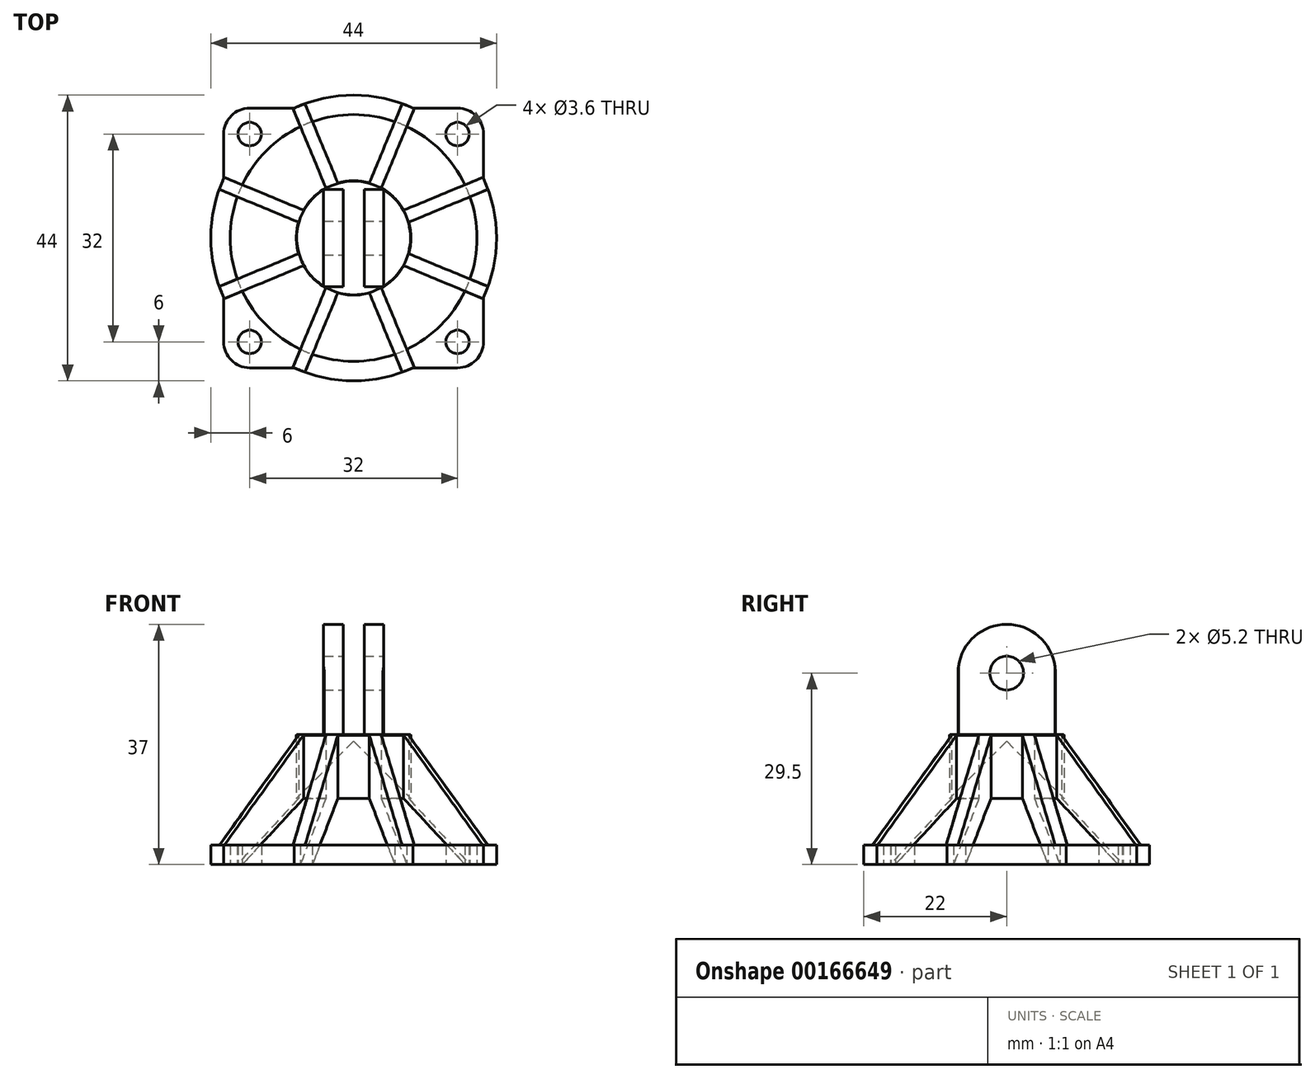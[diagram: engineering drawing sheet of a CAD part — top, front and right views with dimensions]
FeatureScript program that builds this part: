
annotation { "Feature Type Name" : "Feature", "Feature Type Description" : "" }
export const myFeature = defineFeature(function(context is Context, id is Id, definition is map)
    precondition{}
    {
        {
            var Q0;
            Q0=qCreatedBy(makeId("Top.planeOp"),FACE);
            var sketch = newSketch(context, id + "F0", { "sketchPlane" : qUnion([Q0])});
            skLineSegment(sketch, "E0.bottom", {"start": v(16, -16) * mm, "end": v(-16, -16) * mm, "construction": true});
            skLineSegment(sketch, "E0.top", {"start": v(16, 16) * mm, "end": v(-16, 16) * mm, "construction": true});
            skLineSegment(sketch, "E0.left", {"start": v(16, -16) * mm, "end": v(16, 16) * mm, "construction": true});
            skLineSegment(sketch, "E0.right", {"start": v(-16, -16) * mm, "end": v(-16, 16) * mm, "construction": true});
            skPoint(sketch, "E0.middle", {"position": v(0, 0) * mm});
            skLineSegment(sketch, "E1.bottom", {"start": v(16, -20) * mm, "end": v(9.17, -20) * mm});
            skLineSegment(sketch, "E1.top", {"start": v(16, 20) * mm, "end": v(9.17, 20) * mm});
            skLineSegment(sketch, "E1.left", {"start": v(20, -16) * mm, "end": v(20, -9.17) * mm});
            skLineSegment(sketch, "E1.right", {"start": v(-20, -16) * mm, "end": v(-20, -9.17) * mm});
            skCircle(sketch, "E2", {"center": v(0, 0) * mm, "radius": 19 * mm});
            skArc(sketch, "E3", {"start": v(-20, 9.17) * mm, "mid": v(-22, 0) * mm, "end": v(-20, -9.17) * mm});
            skLineSegment(sketch, "E4.trimOffspring", {"start": v(-9.17, 20) * mm, "end": v(-16, 20) * mm});
            skLineSegment(sketch, "E5.trimOffspring", {"start": v(20, 9.17) * mm, "end": v(20, 16) * mm});
            skLineSegment(sketch, "E6.trimOffspring", {"start": v(-9.17, -20) * mm, "end": v(-16, -20) * mm});
            skLineSegment(sketch, "E7.trimOffspring", {"start": v(-20, 9.17) * mm, "end": v(-20, 16) * mm});
            skArc(sketch, "E8.trimOffspring", {"start": v(9.17, 20) * mm, "mid": v(0, 22) * mm, "end": v(-9.17, 20) * mm});
            skArc(sketch, "E9.trimOffspring", {"start": v(20, -9.17) * mm, "mid": v(22, 0) * mm, "end": v(20, 9.17) * mm});
            skArc(sketch, "E10.trimOffspring", {"start": v(-9.17, -20) * mm, "mid": v(0, -22) * mm, "end": v(9.17, -20) * mm});
            skCircle(sketch, "E11", {"center": v(-16, 16) * mm, "radius": 1.8 * mm});
            skCircle(sketch, "E12", {"center": v(16, 16) * mm, "radius": 1.8 * mm});
            skCircle(sketch, "E13", {"center": v(16, -16) * mm, "radius": 1.8 * mm});
            skCircle(sketch, "E14", {"center": v(-16, -16) * mm, "radius": 1.8 * mm});
            skArc(sketch, "E15", {"start": v(20, 16) * mm, "mid": v(18.83, 18.83) * mm, "end": v(16, 20) * mm});
            skArc(sketch, "E16", {"start": v(-16, 20) * mm, "mid": v(-18.83, 18.83) * mm, "end": v(-20, 16) * mm});
            skArc(sketch, "E17", {"start": v(-20, -16) * mm, "mid": v(-18.83, -18.83) * mm, "end": v(-16, -20) * mm});
            skArc(sketch, "E18", {"start": v(16, -20) * mm, "mid": v(18.83, -18.83) * mm, "end": v(20, -16) * mm});
            skPoint(sketch, "E19.orphan", {"position": v(20, 20) * mm});
            skPoint(sketch, "E20.orphan", {"position": v(-20, 20) * mm});
            skPoint(sketch, "E21.orphan", {"position": v(-20, -20) * mm});
            skPoint(sketch, "E22.orphan", {"position": v(20, -20) * mm});
            skSolve(sketch);
        }
        {
            var Q0;
            Q0 = qSketchRegion(id + "F0", true);
            extrude(context, id + "F1", {"entities" : qUnion([Q0]), "depth" : 3 * mm});
        }
        {
            var Q0;
            Q0=qCreatedBy(makeId("Top.planeOp"),FACE);
            var sketch = newSketch(context, id + "F2", { "sketchPlane" : qUnion([Q0])});
            skLineSegment(sketch, "E23.bottom", {"start": v(7.5, -7.5) * mm, "end": v(-7.5, -7.5) * mm});
            skLineSegment(sketch, "E23.top", {"start": v(7.5, 7.5) * mm, "end": v(-7.5, 7.5) * mm});
            skLineSegment(sketch, "E23.left", {"start": v(7.5, -7.5) * mm, "end": v(7.5, 7.5) * mm});
            skLineSegment(sketch, "E23.right", {"start": v(-7.5, -7.5) * mm, "end": v(-7.5, 7.5) * mm});
            skPoint(sketch, "E23.middle", {"position": v(0, 0) * mm});
            skLineSegment(sketch, "E24", {"start": v(0, 0) * mm, "end": v(-20.33, 8.42) * mm, "construction": true});
            skCircle(sketch, "E25", {"center": v(0, 0) * mm, "radius": 22 * mm});
            skCircle(sketch, "E26", {"center": v(0, 0) * mm, "radius": 8.81 * mm});
            skLineSegment(sketch, "E27", {"start": v(-8.47, 2.43) * mm, "end": v(-20.69, 7.49) * mm});
            skLineSegment(sketch, "E28", {"start": v(-7.7, 4.27) * mm, "end": v(-19.92, 9.33) * mm});
            skLineSegment(sketch, "E29.1.1", {"start": v(-7.7, -4.27) * mm, "end": v(-19.92, -9.33) * mm});
            skLineSegment(sketch, "E29.1.2", {"start": v(-8.47, -2.43) * mm, "end": v(-20.69, -7.49) * mm});
            skLineSegment(sketch, "E29.2.1", {"start": v(-2.43, -8.47) * mm, "end": v(-7.49, -20.69) * mm});
            skLineSegment(sketch, "E29.2.2", {"start": v(-4.27, -7.7) * mm, "end": v(-9.33, -19.92) * mm});
            skLineSegment(sketch, "E29.3.1", {"start": v(4.27, -7.7) * mm, "end": v(9.33, -19.92) * mm});
            skLineSegment(sketch, "E29.3.2", {"start": v(2.43, -8.47) * mm, "end": v(7.49, -20.69) * mm});
            skLineSegment(sketch, "E29.4.1", {"start": v(8.47, -2.43) * mm, "end": v(20.69, -7.49) * mm});
            skLineSegment(sketch, "E29.4.2", {"start": v(7.7, -4.27) * mm, "end": v(19.92, -9.33) * mm});
            skLineSegment(sketch, "E29.5.1", {"start": v(7.7, 4.27) * mm, "end": v(19.92, 9.33) * mm});
            skLineSegment(sketch, "E29.5.2", {"start": v(8.47, 2.43) * mm, "end": v(20.69, 7.49) * mm});
            skLineSegment(sketch, "E29.6.1", {"start": v(2.43, 8.47) * mm, "end": v(7.49, 20.69) * mm});
            skLineSegment(sketch, "E29.6.2", {"start": v(4.27, 7.7) * mm, "end": v(9.33, 19.92) * mm});
            skLineSegment(sketch, "E29.7.1", {"start": v(-4.27, 7.7) * mm, "end": v(-9.33, 19.92) * mm});
            skLineSegment(sketch, "E29.7.2", {"start": v(-2.43, 8.47) * mm, "end": v(-7.49, 20.69) * mm});
            skArc(sketch, "E30.0", {"start": v(-20, 9.17) * mm, "mid": v(-22, 0) * mm, "end": v(-20, -9.17) * mm, "construction": true});
            skLineSegment(sketch, "E31", {"start": v(-1.63, 7.5) * mm, "end": v(-1.62, -7.5) * mm, "construction": true});
            skLineSegment(sketch, "E32", {"start": v(-4.62, 7.5) * mm, "end": v(-4.62, -7.5) * mm, "construction": true});
            skPoint(sketch, "E33", {"position": v(0, 7.5) * mm});
            skSolve(sketch);
        }
        {
            var Q0;
            {var subQ0=sQuery(id+"F2.wireOp",EDGE,"E29.7.1");Q0=makeQuery(id+"F2.imprint","IMPRINT",FACE,{"disambiguationData":[TD([[makeQuery(id+"F2.imprint","IMPRINT",EDGE,{"derivedFrom":subQ0}),-1.0]])]});}
            var Q1;
            {var subQ0=sQuery(id+"F2.wireOp",EDGE,"E27");Q1=makeQuery(id+"F2.imprint","IMPRINT",FACE,{"disambiguationData":[TD([[makeQuery(id+"F2.imprint","IMPRINT",EDGE,{"derivedFrom":subQ0}),-1.0]])]});}
            var Q2;
            {var subQ0=sQuery(id+"F2.wireOp",EDGE,"E29.1.1");Q2=makeQuery(id+"F2.imprint","IMPRINT",FACE,{"disambiguationData":[TD([[makeQuery(id+"F2.imprint","IMPRINT",EDGE,{"derivedFrom":subQ0}),-1.0]])]});}
            var Q3;
            {var subQ0=sQuery(id+"F2.wireOp",EDGE,"E29.2.1");Q3=makeQuery(id+"F2.imprint","IMPRINT",FACE,{"disambiguationData":[TD([[makeQuery(id+"F2.imprint","IMPRINT",EDGE,{"derivedFrom":subQ0}),-1.0]])]});}
            var Q4;
            {var subQ0=sQuery(id+"F2.wireOp",EDGE,"E29.3.1");Q4=makeQuery(id+"F2.imprint","IMPRINT",FACE,{"disambiguationData":[TD([[makeQuery(id+"F2.imprint","IMPRINT",EDGE,{"derivedFrom":subQ0}),-1.0]])]});}
            var Q5;
            {var subQ0=sQuery(id+"F2.wireOp",EDGE,"E29.4.1");Q5=makeQuery(id+"F2.imprint","IMPRINT",FACE,{"disambiguationData":[TD([[makeQuery(id+"F2.imprint","IMPRINT",EDGE,{"derivedFrom":subQ0}),-1.0]])]});}
            var Q6;
            {var subQ0=sQuery(id+"F2.wireOp",EDGE,"E29.5.1");Q6=makeQuery(id+"F2.imprint","IMPRINT",FACE,{"disambiguationData":[TD([[makeQuery(id+"F2.imprint","IMPRINT",EDGE,{"derivedFrom":subQ0}),-1.0]])]});}
            var Q7;
            {var subQ0=sQuery(id+"F2.wireOp",EDGE,"E29.6.1");Q7=makeQuery(id+"F2.imprint","IMPRINT",FACE,{"disambiguationData":[TD([[makeQuery(id+"F2.imprint","IMPRINT",EDGE,{"derivedFrom":subQ0}),-1.0]])]});}
            var Q8;
            {var subQ0=sQuery(id+"F2.wireOp",EDGE,"E26");var subQ8=sQuery(id+"F2.wireOp",EDGE,"E23.bottom");var subQ9=makeQuery(id+"F2.imprint","INTERSECT",VERTEX,{"disambiguationData":[OD(0.0)],"derivedFrom":[subQ8,subQ0]});Q8=makeQuery(id+"F2.imprint","IMPRINT",FACE,{"disambiguationData":[TD([[makeQuery(id+"F2.imprint","IMPRINT",EDGE,{"disambiguationData":[TD([[subQ9,-1.0]])],"derivedFrom":subQ8}),-1.0]])]});}
            var Q9;
            {var subQ0=sQuery(id+"F2.wireOp",EDGE,"E26");var subQ4=sQuery(id+"F2.wireOp",EDGE,"E23.top");var subQ5=makeQuery(id+"F2.imprint","INTERSECT",VERTEX,{"disambiguationData":[OD(0.0)],"derivedFrom":[subQ4,subQ0]});Q9=makeQuery(id+"F2.imprint","IMPRINT",FACE,{"disambiguationData":[TD([[makeQuery(id+"F2.imprint","IMPRINT",EDGE,{"disambiguationData":[TD([[subQ5,-1.0]])],"derivedFrom":subQ4}),-1.0]])]});}
            var Q10;
            {var subQ0=sQuery(id+"F2.wireOp",EDGE,"E26");var subQ2=sQuery(id+"F2.wireOp",EDGE,"E23.left");var subQ3=makeQuery(id+"F2.imprint","INTERSECT",VERTEX,{"disambiguationData":[OD(0.0)],"derivedFrom":[subQ2,subQ0]});Q10=makeQuery(id+"F2.imprint","IMPRINT",FACE,{"disambiguationData":[TD([[makeQuery(id+"F2.imprint","IMPRINT",EDGE,{"disambiguationData":[TD([[subQ3,-1.0]])],"derivedFrom":subQ2}),-1.0]])]});}
            var Q11;
            {var subQ0=sQuery(id+"F2.wireOp",EDGE,"E26");var subQ5=sQuery(id+"F2.wireOp",EDGE,"E23.bottom");var subQ7=makeQuery(id+"F2.imprint","INTERSECT",VERTEX,{"disambiguationData":[OD(0.0)],"derivedFrom":[subQ5,subQ0]});Q11=makeQuery(id+"F2.imprint","IMPRINT",FACE,{"disambiguationData":[TD([[makeQuery(id+"F2.imprint","IMPRINT",EDGE,{"disambiguationData":[TD([[subQ7,-1.0]])],"derivedFrom":subQ5}),1.0]])]});}
            var Q12;
            {var subQ0=sQuery(id+"F2.wireOp",EDGE,"E26");var subQ4=sQuery(id+"F2.wireOp",EDGE,"E23.right");var subQ6=makeQuery(id+"F2.imprint","INTERSECT",VERTEX,{"disambiguationData":[OD(0.0)],"derivedFrom":[subQ4,subQ0]});Q12=makeQuery(id+"F2.imprint","IMPRINT",FACE,{"disambiguationData":[TD([[makeQuery(id+"F2.imprint","IMPRINT",EDGE,{"disambiguationData":[TD([[subQ6,-1.0]])],"derivedFrom":subQ4}),1.0]])]});}
            extrude(context, id + "F3", {"entities" : qUnion([Q0, Q1, Q2, Q3, Q4, Q5, Q6, Q7, Q8, Q9, Q10, Q11, Q12]), "operationType" : NewBodyOperationType.ADD, "depth" : 20 * mm});
        }
        {
            var Q0;
            Q0=qCreatedBy(makeId("Front.planeOp"),FACE);
            var sketch = newSketch(context, id + "F4", { "sketchPlane" : qUnion([Q0])});
            skPoint(sketch, "E34.0", {"position": v(0, 0) * mm});
            skPoint(sketch, "E34.1", {"position": v(-19, 0) * mm});
            skLineSegment(sketch, "E35", {"start": v(-19, 0) * mm, "end": v(0, 0) * mm});
            skLineSegment(sketch, "E36", {"start": v(0, 0) * mm, "end": v(0, 19) * mm});
            skLineSegment(sketch, "E37", {"start": v(0, 19) * mm, "end": v(-19, 0) * mm});
            skSolve(sketch);
        }
        {
            var Q0;
            Q0=makeQuery(id+"F4.imprint","IMPRINT",FACE,{"disambiguationData":[TD([[makeQuery(id+"F4.imprint","IMPRINT",EDGE,{"derivedFrom":sQuery(id+"F4.wireOp",EDGE,"E35")}),1.0]])]});
            var Q1;
            Q1=sQuery(id+"F4.wireOp",EDGE,"E36");
            revolve(context, id + "F5", {"operationType" : NewBodyOperationType.REMOVE, "entities" : qUnion([Q0]), "axis" : qUnion([Q1]), "revolveType" : RevolveType.FULL, "oppositeDirection" : true});
        }
        {
            var Q0;
            Q0=makeQuery(id+"F3.opExtrude","SWEPT_FACE",FACE,{"disambiguationData":[OSD([sQuery(id+"F2.wireOp",EDGE,"E29.2.1")])]});
            var Q1;
            Q1=makeQuery(id+"F3.opExtrude","SWEPT_FACE",FACE,{"disambiguationData":[OSD([sQuery(id+"F2.wireOp",EDGE,"E29.2.2")])]});
            cPlane(context, id + "F6", {"entities" : qUnion([Q0, Q1]), "cplaneType" : CPlaneType.MID_PLANE, "offset" : 25 * mm, "width" : 150 * mm, "height" : 150 * mm});
        }
        {
            var Q0;
            Q0=qCreatedBy(id+"F6.planeOp",FACE);
            var sketch = newSketch(context, id + "F7", { "sketchPlane" : qUnion([Q0])});
            skPoint(sketch, "E38.0", {"position": v(-21.98, 3) * mm});
            skPoint(sketch, "E38.1", {"position": v(-8.75, 20) * mm});
            skPoint(sketch, "E39.0", {"position": v(-21.98, 20) * mm});
            skLineSegment(sketch, "E40", {"start": v(0, 0) * mm, "end": v(0, 20.24) * mm, "construction": true});
            skLineSegment(sketch, "E41", {"start": v(-21.98, 3) * mm, "end": v(-8.75, 20) * mm});
            skLineSegment(sketch, "E42", {"start": v(-21.98, 20) * mm, "end": v(-8.75, 20) * mm});
            skLineSegment(sketch, "E43", {"start": v(-21.98, 3) * mm, "end": v(-22.48, 3) * mm});
            skLineSegment(sketch, "E44", {"start": v(-22.48, 3) * mm, "end": v(-22.48, 20) * mm});
            skLineSegment(sketch, "E45", {"start": v(-22.48, 20) * mm, "end": v(-21.98, 20) * mm});
            skSolve(sketch);
        }
        {
            var Q0;
            Q0=makeQuery(id+"F7.imprint","IMPRINT",FACE,{"disambiguationData":[TD([[makeQuery(id+"F7.imprint","IMPRINT",EDGE,{"derivedFrom":sQuery(id+"F7.wireOp",EDGE,"E41")}),1.0]])]});
            var Q1;
            Q1=sQuery(id+"F7.wireOp",EDGE,"E40");
            revolve(context, id + "F8", {"operationType" : NewBodyOperationType.REMOVE, "entities" : qUnion([Q0]), "axis" : qUnion([Q1]), "revolveType" : RevolveType.FULL, "oppositeDirection" : true});
        }
        {
            var Q0;
            {var subQ0=sQuery(id+"F2.wireOp",EDGE,"E26");var subQ1=sQuery(id+"F2.wireOp",EDGE,"E25");Q0=makeQuery(id+"FryXNGp9iaOWU7Y_1.boolean.opBoolean","MERGE",FACE,{"derivedFrom":[makeQuery(id+"F3.opExtrude","CAP_FACE",FACE,{"disambiguationData":[OSD([subQ1,subQ0,sQuery(id+"F2.wireOp",EDGE,"E29.5.1"),sQuery(id+"F2.wireOp",EDGE,"E29.5.2")])],"isStart":false}),makeQuery(id+"F3.opExtrude","CAP_FACE",FACE,{"disambiguationData":[OSD([subQ1,subQ0,sQuery(id+"F2.wireOp",EDGE,"E29.6.1"),sQuery(id+"F2.wireOp",EDGE,"E29.6.2")])],"isStart":false}),makeQuery(id+"F3.opExtrude","CAP_FACE",FACE,{"disambiguationData":[OSD([subQ1,subQ0,sQuery(id+"F2.wireOp",EDGE,"E29.7.1"),sQuery(id+"F2.wireOp",EDGE,"E29.7.2")])],"isStart":false}),makeQuery(id+"F3.opExtrude","CAP_FACE",FACE,{"disambiguationData":[OSD([subQ1,subQ0,sQuery(id+"F2.wireOp",EDGE,"E27"),sQuery(id+"F2.wireOp",EDGE,"E28")])],"isStart":false}),makeQuery(id+"F3.opExtrude","CAP_FACE",FACE,{"disambiguationData":[OSD([subQ1,subQ0,sQuery(id+"F2.wireOp",EDGE,"E29.1.1"),sQuery(id+"F2.wireOp",EDGE,"E29.1.2")])],"isStart":false}),makeQuery(id+"F3.opExtrude","CAP_FACE",FACE,{"disambiguationData":[OSD([subQ1,subQ0,sQuery(id+"F2.wireOp",EDGE,"E29.2.1"),sQuery(id+"F2.wireOp",EDGE,"E29.2.2")])],"isStart":false}),makeQuery(id+"F3.opExtrude","CAP_FACE",FACE,{"disambiguationData":[OSD([subQ1,subQ0,sQuery(id+"F2.wireOp",EDGE,"E29.3.1"),sQuery(id+"F2.wireOp",EDGE,"E29.3.2")])],"isStart":false}),makeQuery(id+"F3.opExtrude","CAP_FACE",FACE,{"disambiguationData":[OSD([subQ1,subQ0,sQuery(id+"F2.wireOp",EDGE,"E29.4.1"),sQuery(id+"F2.wireOp",EDGE,"E29.4.2")])],"isStart":false}),makeQuery(id+"FryXNGp9iaOWU7Y_1.opExtrude","CAP_FACE",FACE,{"disambiguationData":[OSD([subQ0])],"isStart":false})]});}
            var sketch = newSketch(context, id + "F9", { "sketchPlane" : qUnion([Q0])});
            skLineSegment(sketch, "E46.0", {"start": v(-7.5, -7.5) * mm, "end": v(-7.5, 7.5) * mm});
            skLineSegment(sketch, "E46.1", {"start": v(7.5, -7.5) * mm, "end": v(-7.5, -7.5) * mm});
            skLineSegment(sketch, "E46.2", {"start": v(7.5, -7.5) * mm, "end": v(7.5, 7.5) * mm});
            skLineSegment(sketch, "E46.3", {"start": v(7.5, 7.5) * mm, "end": v(-7.5, 7.5) * mm});
            skPoint(sketch, "E46.4", {"position": v(0, 0) * mm});
            skLineSegment(sketch, "E47", {"start": v(-1.62, 7.5) * mm, "end": v(-1.63, -7.5) * mm});
            skLineSegment(sketch, "E48", {"start": v(-4.62, 7.5) * mm, "end": v(-4.63, -7.5) * mm});
            skLineSegment(sketch, "E49", {"start": v(1.62, 7.5) * mm, "end": v(1.63, -7.5) * mm});
            skLineSegment(sketch, "E50", {"start": v(4.62, 7.5) * mm, "end": v(4.63, -7.5) * mm});
            skSolve(sketch);
        }
        {
            var Q0;
            {var subQ0=sQuery(id+"F9.wireOp",EDGE,"E47");var subQ1=sQuery(id+"F9.wireOp",EDGE,"E46.3");var subQ2=makeQuery(id+"F9.imprint","INTERSECT",VERTEX,{"derivedFrom":[subQ1,subQ0]});Q0=makeQuery(id+"F9.imprint","IMPRINT",FACE,{"disambiguationData":[TD([[makeQuery(id+"F9.imprint","IMPRINT",EDGE,{"disambiguationData":[TD([[subQ2,-1.0]])],"derivedFrom":subQ1}),1.0]])]});}
            var Q1;
            {var subQ0=sQuery(id+"F9.wireOp",EDGE,"E47");var subQ1=sQuery(id+"F2.wireOp",EDGE,"E26");var subQ2=sQuery(id+"F2.wireOp",EDGE,"E25");var subQ3=sQuery(id+"F2.wireOp",EDGE,"E29.2.2");var subQ4=sQuery(id+"F2.wireOp",EDGE,"E29.2.1");var subQ5=sQuery(id+"F2.wireOp",EDGE,"E29.7.2");var subQ6=sQuery(id+"F2.wireOp",EDGE,"E29.7.1");var subQ7=makeQuery(id+"FryXNGp9iaOWU7Y_1.boolean.opBoolean","MERGE",FACE,{"derivedFrom":[makeQuery(id+"F3.opExtrude","CAP_FACE",FACE,{"disambiguationData":[OSD([subQ2,subQ1,sQuery(id+"F2.wireOp",EDGE,"E29.5.1"),sQuery(id+"F2.wireOp",EDGE,"E29.5.2")])],"isStart":false}),makeQuery(id+"F3.opExtrude","CAP_FACE",FACE,{"disambiguationData":[OSD([subQ2,subQ1,sQuery(id+"F2.wireOp",EDGE,"E29.6.1"),sQuery(id+"F2.wireOp",EDGE,"E29.6.2")])],"isStart":false}),makeQuery(id+"F3.opExtrude","CAP_FACE",FACE,{"disambiguationData":[OSD([subQ2,subQ1,subQ6,subQ5])],"isStart":false}),makeQuery(id+"F3.opExtrude","CAP_FACE",FACE,{"disambiguationData":[OSD([subQ2,subQ1,sQuery(id+"F2.wireOp",EDGE,"E27"),sQuery(id+"F2.wireOp",EDGE,"E28")])],"isStart":false}),makeQuery(id+"F3.opExtrude","CAP_FACE",FACE,{"disambiguationData":[OSD([subQ2,subQ1,sQuery(id+"F2.wireOp",EDGE,"E29.1.1"),sQuery(id+"F2.wireOp",EDGE,"E29.1.2")])],"isStart":false}),makeQuery(id+"F3.opExtrude","CAP_FACE",FACE,{"disambiguationData":[OSD([subQ2,subQ1,subQ4,subQ3])],"isStart":false}),makeQuery(id+"F3.opExtrude","CAP_FACE",FACE,{"disambiguationData":[OSD([subQ2,subQ1,sQuery(id+"F2.wireOp",EDGE,"E29.3.1"),sQuery(id+"F2.wireOp",EDGE,"E29.3.2")])],"isStart":false}),makeQuery(id+"F3.opExtrude","CAP_FACE",FACE,{"disambiguationData":[OSD([subQ2,subQ1,sQuery(id+"F2.wireOp",EDGE,"E29.4.1"),sQuery(id+"F2.wireOp",EDGE,"E29.4.2")])],"isStart":false}),makeQuery(id+"FryXNGp9iaOWU7Y_1.opExtrude","CAP_FACE",FACE,{"disambiguationData":[OSD([subQ1])],"isStart":false})]});var subQ8=makeQuery(id+"FLweHT1gDxulgPf_1.opChamfer","BLEND_EDGE",EDGE,{"blendedFrom":[makeQuery(id+"F3.opExtrude","CAP_EDGE",EDGE,{"disambiguationData":[OSD([subQ2]),TDD([makeQuery(id+"F2.imprint","IMPRINT",EDGE,{"disambiguationData":[TD([[makeQuery(id+"F2.imprint","INTERSECT",VERTEX,{"derivedFrom":[subQ2,subQ6]}),1.0]])],"derivedFrom":subQ2})])],"isStart":false}),subQ7],"blendedInto":[subQ7]});var subQ9=makeQuery(id+"F9.imprint","INTERSECT",VERTEX,{"derivedFrom":[subQ8,subQ0]});Q1=makeQuery(id+"F9.imprint","IMPRINT",FACE,{"disambiguationData":[TD([[makeQuery(id+"F9.imprint","IMPRINT",EDGE,{"disambiguationData":[TD([[subQ9,-1.0]])],"derivedFrom":subQ0}),-1.0]])]});}
            var Q2;
            {var subQ0=sQuery(id+"F9.wireOp",EDGE,"E47");var subQ1=sQuery(id+"F9.wireOp",EDGE,"E46.1");var subQ2=makeQuery(id+"F9.imprint","INTERSECT",VERTEX,{"derivedFrom":[subQ1,subQ0]});Q2=makeQuery(id+"F9.imprint","IMPRINT",FACE,{"disambiguationData":[TD([[makeQuery(id+"F9.imprint","IMPRINT",EDGE,{"disambiguationData":[TD([[subQ2,-1.0]])],"derivedFrom":subQ1}),-1.0]])]});}
            var Q3;
            {var subQ0=sQuery(id+"F9.wireOp",EDGE,"E49");var subQ1=sQuery(id+"F2.wireOp",EDGE,"E26");var subQ2=sQuery(id+"F2.wireOp",EDGE,"E25");var subQ3=sQuery(id+"F2.wireOp",EDGE,"E29.3.2");var subQ4=sQuery(id+"F2.wireOp",EDGE,"E29.3.1");var subQ5=sQuery(id+"F2.wireOp",EDGE,"E29.6.2");var subQ6=sQuery(id+"F2.wireOp",EDGE,"E29.6.1");var subQ7=makeQuery(id+"FryXNGp9iaOWU7Y_1.boolean.opBoolean","MERGE",FACE,{"derivedFrom":[makeQuery(id+"F3.opExtrude","CAP_FACE",FACE,{"disambiguationData":[OSD([subQ2,subQ1,sQuery(id+"F2.wireOp",EDGE,"E29.5.1"),sQuery(id+"F2.wireOp",EDGE,"E29.5.2")])],"isStart":false}),makeQuery(id+"F3.opExtrude","CAP_FACE",FACE,{"disambiguationData":[OSD([subQ2,subQ1,subQ6,subQ5])],"isStart":false}),makeQuery(id+"F3.opExtrude","CAP_FACE",FACE,{"disambiguationData":[OSD([subQ2,subQ1,sQuery(id+"F2.wireOp",EDGE,"E29.7.1"),sQuery(id+"F2.wireOp",EDGE,"E29.7.2")])],"isStart":false}),makeQuery(id+"F3.opExtrude","CAP_FACE",FACE,{"disambiguationData":[OSD([subQ2,subQ1,sQuery(id+"F2.wireOp",EDGE,"E27"),sQuery(id+"F2.wireOp",EDGE,"E28")])],"isStart":false}),makeQuery(id+"F3.opExtrude","CAP_FACE",FACE,{"disambiguationData":[OSD([subQ2,subQ1,sQuery(id+"F2.wireOp",EDGE,"E29.1.1"),sQuery(id+"F2.wireOp",EDGE,"E29.1.2")])],"isStart":false}),makeQuery(id+"F3.opExtrude","CAP_FACE",FACE,{"disambiguationData":[OSD([subQ2,subQ1,sQuery(id+"F2.wireOp",EDGE,"E29.2.1"),sQuery(id+"F2.wireOp",EDGE,"E29.2.2")])],"isStart":false}),makeQuery(id+"F3.opExtrude","CAP_FACE",FACE,{"disambiguationData":[OSD([subQ2,subQ1,subQ4,subQ3])],"isStart":false}),makeQuery(id+"F3.opExtrude","CAP_FACE",FACE,{"disambiguationData":[OSD([subQ2,subQ1,sQuery(id+"F2.wireOp",EDGE,"E29.4.1"),sQuery(id+"F2.wireOp",EDGE,"E29.4.2")])],"isStart":false}),makeQuery(id+"FryXNGp9iaOWU7Y_1.opExtrude","CAP_FACE",FACE,{"disambiguationData":[OSD([subQ1])],"isStart":false})]});var subQ8=makeQuery(id+"FLweHT1gDxulgPf_1.opChamfer","BLEND_EDGE",EDGE,{"blendedFrom":[makeQuery(id+"F3.opExtrude","CAP_EDGE",EDGE,{"disambiguationData":[OSD([subQ2]),TDD([makeQuery(id+"F2.imprint","IMPRINT",EDGE,{"disambiguationData":[TD([[makeQuery(id+"F2.imprint","INTERSECT",VERTEX,{"derivedFrom":[subQ2,subQ6]}),1.0]])],"derivedFrom":subQ2})])],"isStart":false}),subQ7],"blendedInto":[subQ7]});var subQ9=makeQuery(id+"F9.imprint","INTERSECT",VERTEX,{"derivedFrom":[subQ8,subQ0]});Q3=makeQuery(id+"F9.imprint","IMPRINT",FACE,{"disambiguationData":[TD([[makeQuery(id+"F9.imprint","IMPRINT",EDGE,{"disambiguationData":[TD([[subQ9,-1.0]])],"derivedFrom":subQ0}),1.0]])]});}
            var Q4;
            {var subQ0=sQuery(id+"F9.wireOp",EDGE,"E49");var subQ1=sQuery(id+"F9.wireOp",EDGE,"E46.3");var subQ2=makeQuery(id+"F9.imprint","INTERSECT",VERTEX,{"derivedFrom":[subQ1,subQ0]});Q4=makeQuery(id+"F9.imprint","IMPRINT",FACE,{"disambiguationData":[TD([[makeQuery(id+"F9.imprint","IMPRINT",EDGE,{"disambiguationData":[TD([[subQ2,1.0]])],"derivedFrom":subQ1}),1.0]])]});}
            var Q5;
            {var subQ0=sQuery(id+"F9.wireOp",EDGE,"E49");var subQ1=sQuery(id+"F9.wireOp",EDGE,"E46.1");var subQ2=makeQuery(id+"F9.imprint","INTERSECT",VERTEX,{"derivedFrom":[subQ1,subQ0]});Q5=makeQuery(id+"F9.imprint","IMPRINT",FACE,{"disambiguationData":[TD([[makeQuery(id+"F9.imprint","IMPRINT",EDGE,{"disambiguationData":[TD([[subQ2,1.0]])],"derivedFrom":subQ1}),-1.0]])]});}
            var Q6;
            Q6=makeQuery(id+"F1.opExtrude","SWEPT_BODY",BODY,{"disambiguationData":[OSD([sQuery(id+"F0.wireOp",EDGE,"E1.bottom"),sQuery(id+"F0.wireOp",EDGE,"E1.top"),sQuery(id+"F0.wireOp",EDGE,"E1.left"),sQuery(id+"F0.wireOp",EDGE,"E1.right"),sQuery(id+"F0.wireOp",EDGE,"E2"),sQuery(id+"F0.wireOp",EDGE,"E3"),sQuery(id+"F0.wireOp",EDGE,"E4.trimOffspring"),sQuery(id+"F0.wireOp",EDGE,"E5.trimOffspring"),sQuery(id+"F0.wireOp",EDGE,"E6.trimOffspring"),sQuery(id+"F0.wireOp",EDGE,"E7.trimOffspring"),sQuery(id+"F0.wireOp",EDGE,"E8.trimOffspring"),sQuery(id+"F0.wireOp",EDGE,"E9.trimOffspring"),sQuery(id+"F0.wireOp",EDGE,"E10.trimOffspring"),sQuery(id+"F0.wireOp",EDGE,"E11"),sQuery(id+"F0.wireOp",EDGE,"E12"),sQuery(id+"F0.wireOp",EDGE,"E13"),sQuery(id+"F0.wireOp",EDGE,"E14"),sQuery(id+"F0.wireOp",EDGE,"E15"),sQuery(id+"F0.wireOp",EDGE,"E16"),sQuery(id+"F0.wireOp",EDGE,"E17"),sQuery(id+"F0.wireOp",EDGE,"E18")])]});
            extrude(context, id + "F10", {"entities" : qUnion([Q0, Q1, Q2, Q3, Q4, Q5]), "operationType" : NewBodyOperationType.ADD, "depth" : 17 * mm, "hasSecondDirection" : true, "secondDirectionOppositeDirection" : true, "secondDirectionBoundEntityBody" : qUnion([Q6]), "secondDirectionDepth" : 1 * mm});
        }
        {
            var Q0;
            Q0=makeQuery(id+"F10.opExtrude","SWEPT_FACE",FACE,{"disambiguationData":[OSD([sQuery(id+"F9.wireOp",EDGE,"E50")])]});
            var sketch = newSketch(context, id + "F11", { "sketchPlane" : qUnion([Q0])});
            skCircle(sketch, "E51", {"center": v(0, 29.5) * mm, "radius": 7.5 * mm});
            skPoint(sketch, "E51.centerSnap0", {"position": v(0, 37) * mm});
            skCircle(sketch, "E52", {"center": v(0, 29.5) * mm, "radius": 2.6 * mm});
            skLineSegment(sketch, "E53", {"start": v(-7.5, 29.5) * mm, "end": v(-7.5, 37) * mm});
            skLineSegment(sketch, "E54", {"start": v(-7.5, 37) * mm, "end": v(-7.43, 37) * mm});
            skLineSegment(sketch, "E55", {"start": v(7.5, 29.5) * mm, "end": v(7.5, 37) * mm});
            skLineSegment(sketch, "E56", {"start": v(7.5, 37) * mm, "end": v(7.43, 37) * mm});
            skSolve(sketch);
        }
        {
            var Q0;
            {var subQ0=sQuery(id+"F11.wireOp",EDGE,"E51");var subQ1=sQuery(id+"F9.wireOp",EDGE,"E50");var subQ2=makeQuery(id+"F10.opExtrude","CAP_EDGE",EDGE,{"disambiguationData":[OSD([subQ1])],"isStart":false});var subQ3=makeQuery(id+"F11.imprint","INTERSECT",VERTEX,{"derivedFrom":[subQ2,subQ0]});Q0=makeQuery(id+"F11.imprint","IMPRINT",FACE,{"disambiguationData":[TD([[makeQuery(id+"F11.imprint","IMPRINT",EDGE,{"disambiguationData":[TD([[subQ3,-1.0]])],"derivedFrom":subQ0}),-1.0]])]});}
            var Q1;
            {var subQ0=sQuery(id+"F11.wireOp",EDGE,"E51");var subQ1=sQuery(id+"F9.wireOp",EDGE,"E50");var subQ2=makeQuery(id+"F10.opExtrude","CAP_EDGE",EDGE,{"disambiguationData":[OSD([subQ1])],"isStart":false});var subQ3=makeQuery(id+"F11.imprint","INTERSECT",VERTEX,{"derivedFrom":[subQ2,subQ0]});Q1=makeQuery(id+"F11.imprint","IMPRINT",FACE,{"disambiguationData":[TD([[makeQuery(id+"F11.imprint","IMPRINT",EDGE,{"disambiguationData":[TD([[subQ3,1.0]])],"derivedFrom":subQ0}),-1.0]])]});}
            var Q2;
            Q2=makeQuery(id+"F11.imprint","IMPRINT",FACE,{"disambiguationData":[TD([[makeQuery(id+"F11.imprint","IMPRINT",EDGE,{"derivedFrom":sQuery(id+"F11.wireOp",EDGE,"E52")}),1.0]])]});
            var Q3;
            {var subQ0=sQuery(id+"F11.wireOp",EDGE,"E53");Q3=makeQuery(id+"F11.imprint","IMPRINT",FACE,{"disambiguationData":[TD([[makeQuery(id+"F11.imprint","IMPRINT",EDGE,{"derivedFrom":subQ0}),-1.0]])]});}
            var Q4;
            {var subQ0=sQuery(id+"F11.wireOp",EDGE,"E55");Q4=makeQuery(id+"F11.imprint","IMPRINT",FACE,{"disambiguationData":[TD([[makeQuery(id+"F11.imprint","IMPRINT",EDGE,{"derivedFrom":subQ0}),1.0]])]});}
            extrude(context, id + "F12", {"entities" : qUnion([Q0, Q1, Q2, Q3, Q4]), "operationType" : NewBodyOperationType.REMOVE, "endBound" : BoundingType.THROUGH_ALL, "oppositeDirection" : true, "depth" : 25 * mm});
        }
    });
